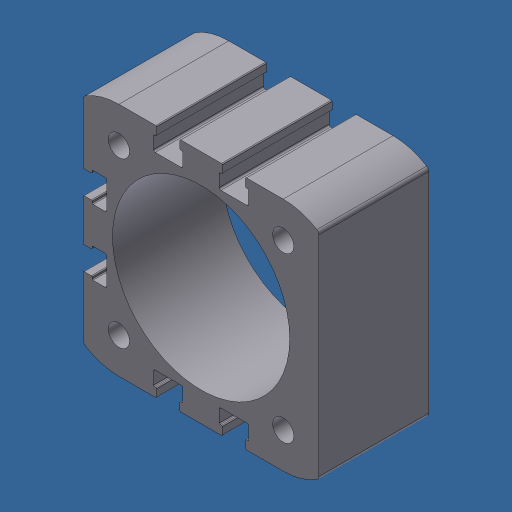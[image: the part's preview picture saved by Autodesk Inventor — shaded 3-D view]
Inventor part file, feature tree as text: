
AUTODESK INVENTOR PART (.ipt)
format: ipt  version: 2024.3 (Build 283343000, 343)  size: 291,840 bytes
history: native  units: mm (DEFAULTED — no unit token found)
features: other x1, sketch x1, extrude x1, hole x1
ambient origin geometry x8: Origin, YZ Plane, XZ Plane, XY Plane, X Axis, Y Axis, Z Axis, Center Point
bodies: Body1 (feature_tree)
feature tree (4):
  other  "Finish - None"
  sketch  "Sketch1"  dims[d1=41.0mm d2=25.4mm d3=0.0mm d4=4.91mm d5=12.7mm d6=9.525mm d7=6.35mm d8=14.3117mm d9=19.05mm d10=20.594885mm]
  extrude  "FESTO, 40MM"  Depth=25.4mm TaperAngle=0.0deg
  hole  "Hole1"  [1 undecoded]
note: 1 required parameter value undecoded (feature->parameter linkage not recoverable at this tier; creation-order binding heuristic only, values carry confidence <= 0.55)
